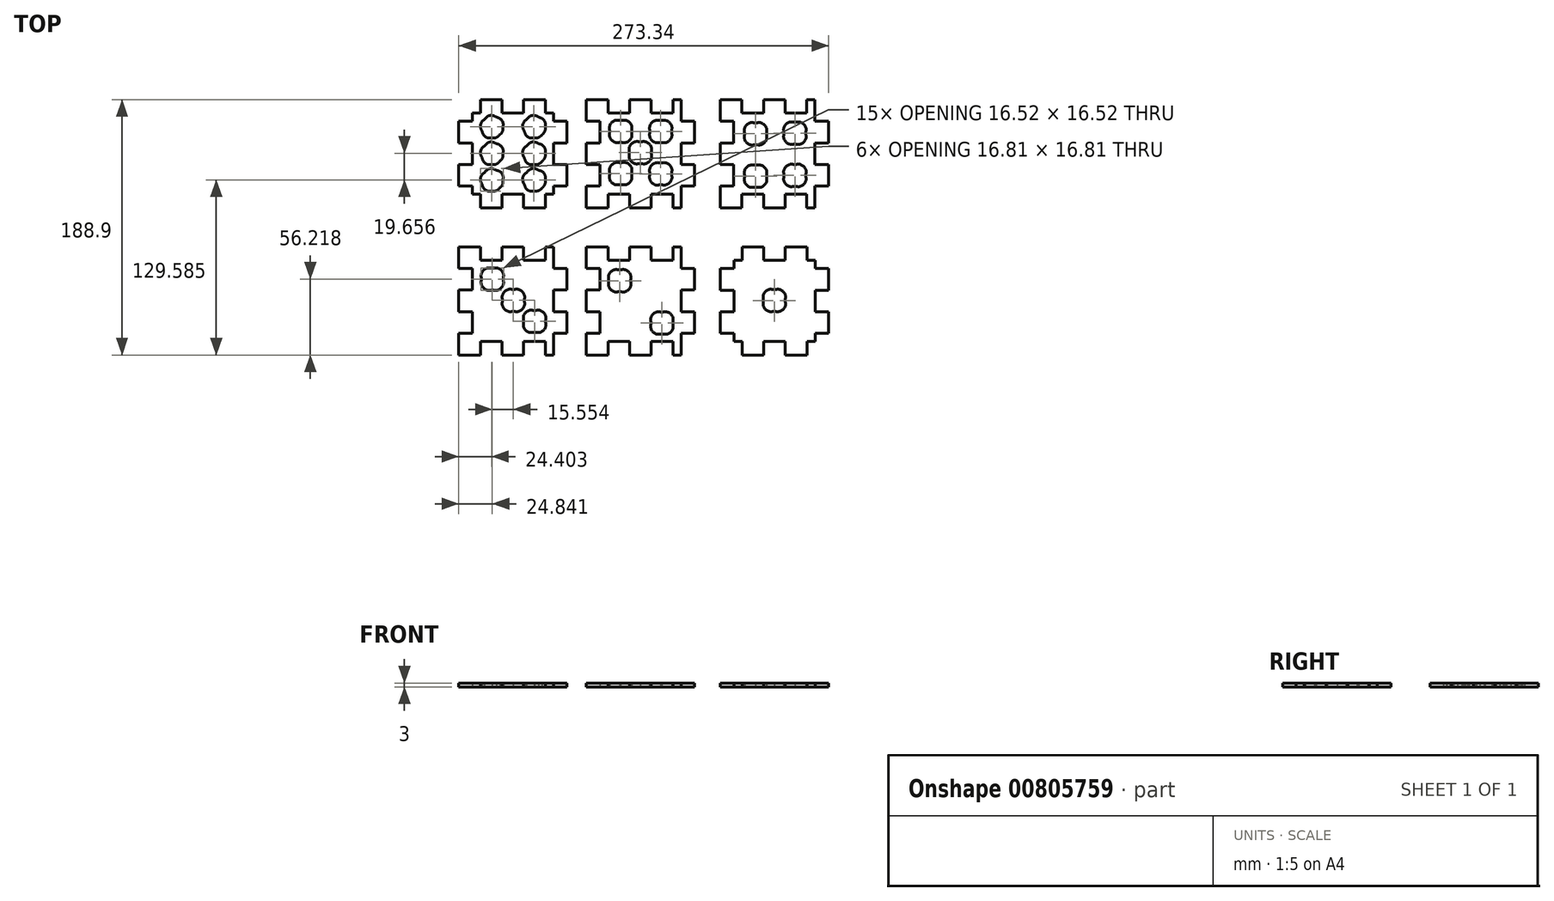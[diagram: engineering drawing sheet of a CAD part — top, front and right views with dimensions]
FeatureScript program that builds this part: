
annotation { "Feature Type Name" : "Feature", "Feature Type Description" : "" }
export const myFeature = defineFeature(function(context is Context, id is Id, definition is map)
    precondition{}
    {
        {
            var Q0;
            Q0=qCreatedBy(makeId("Top.planeOp"),FACE);
            var sketch = newSketch(context, id + "F0", { "sketchPlane" : qUnion([Q0])});
            skLineSegment(sketch, "E0", {"start": v(-126.67, 24.45) * mm, "end": v(-120.67, 24.45) * mm});
            skLineSegment(sketch, "E1", {"start": v(-120.67, 24.45) * mm, "end": v(-120.67, 14.45) * mm});
            skLineSegment(sketch, "E2", {"start": v(-120.67, 14.45) * mm, "end": v(-104.67, 14.45) * mm});
            skLineSegment(sketch, "E3", {"start": v(-104.67, 24.45) * mm, "end": v(-104.67, 14.45) * mm});
            skLineSegment(sketch, "E4", {"start": v(-104.67, 24.45) * mm, "end": v(-88.67, 24.45) * mm});
            skLineSegment(sketch, "E5", {"start": v(-88.67, 24.45) * mm, "end": v(-88.67, 14.45) * mm});
            skLineSegment(sketch, "E6", {"start": v(-88.67, 14.45) * mm, "end": v(-72.67, 14.45) * mm});
            skLineSegment(sketch, "E7", {"start": v(-72.67, 24.45) * mm, "end": v(-72.67, 14.45) * mm});
            skLineSegment(sketch, "E8", {"start": v(-72.67, 24.45) * mm, "end": v(-66.67, 24.45) * mm});
            skLineSegment(sketch, "E9", {"start": v(-126.67, 84.45) * mm, "end": v(-120.67, 84.45) * mm});
            skLineSegment(sketch, "E10", {"start": v(-120.67, 94.45) * mm, "end": v(-120.67, 84.45) * mm});
            skLineSegment(sketch, "E11", {"start": v(-120.67, 94.45) * mm, "end": v(-104.67, 94.45) * mm});
            skLineSegment(sketch, "E12", {"start": v(-104.67, 94.45) * mm, "end": v(-104.67, 84.45) * mm});
            skLineSegment(sketch, "E13", {"start": v(-104.67, 84.45) * mm, "end": v(-88.67, 84.45) * mm});
            skLineSegment(sketch, "E14", {"start": v(-88.67, 94.45) * mm, "end": v(-88.67, 84.45) * mm});
            skLineSegment(sketch, "E15", {"start": v(-88.67, 94.45) * mm, "end": v(-72.67, 94.45) * mm});
            skLineSegment(sketch, "E16", {"start": v(-72.67, 94.45) * mm, "end": v(-72.67, 84.45) * mm});
            skLineSegment(sketch, "E17", {"start": v(-72.67, 84.45) * mm, "end": v(-66.67, 84.45) * mm});
            skLineSegment(sketch, "E18", {"start": v(-126.67, 24.45) * mm, "end": v(-126.67, 30.45) * mm});
            skLineSegment(sketch, "E19", {"start": v(-126.67, 30.45) * mm, "end": v(-136.67, 30.45) * mm});
            skLineSegment(sketch, "E20", {"start": v(-136.67, 30.45) * mm, "end": v(-136.67, 46.45) * mm});
            skLineSegment(sketch, "E21", {"start": v(-126.67, 46.45) * mm, "end": v(-136.67, 46.45) * mm});
            skLineSegment(sketch, "E22", {"start": v(-126.67, 46.45) * mm, "end": v(-126.67, 62.45) * mm});
            skLineSegment(sketch, "E23", {"start": v(-126.67, 62.45) * mm, "end": v(-136.67, 62.45) * mm});
            skLineSegment(sketch, "E24", {"start": v(-136.67, 62.45) * mm, "end": v(-136.67, 78.45) * mm});
            skLineSegment(sketch, "E25", {"start": v(-126.67, 78.45) * mm, "end": v(-136.67, 78.45) * mm});
            skLineSegment(sketch, "E26", {"start": v(-126.67, 78.45) * mm, "end": v(-126.67, 84.45) * mm});
            skLineSegment(sketch, "E27", {"start": v(-66.67, 24.45) * mm, "end": v(-66.67, 30.45) * mm});
            skLineSegment(sketch, "E28", {"start": v(-56.67, 30.45) * mm, "end": v(-66.67, 30.45) * mm});
            skLineSegment(sketch, "E29", {"start": v(-56.67, 30.45) * mm, "end": v(-56.67, 46.45) * mm});
            skLineSegment(sketch, "E30", {"start": v(-56.67, 46.45) * mm, "end": v(-66.67, 46.45) * mm});
            skLineSegment(sketch, "E31", {"start": v(-66.67, 46.45) * mm, "end": v(-66.67, 62.45) * mm});
            skLineSegment(sketch, "E32", {"start": v(-56.67, 62.45) * mm, "end": v(-66.67, 62.45) * mm});
            skFitSpline(sketch, "E33", {"points": [v(-104, 74.18) * mm, v(-104, 72.06) * mm, v(-104.84, 70.02) * mm, v(-106.34, 68.52) * mm]});
            skFitSpline(sketch, "E34", {"points": [v(-106.34, 68.52) * mm, v(-107.84, 67.02) * mm, v(-109.88, 66.18) * mm, v(-112, 66.18) * mm]});
            skFitSpline(sketch, "E35", {"points": [v(-112, 66.18) * mm, v(-115.23, 66.18) * mm, v(-118.15, 68.13) * mm, v(-119.39, 71.12) * mm]});
            skFitSpline(sketch, "E36", {"points": [v(-119.39, 71.12) * mm, v(-120.63, 74.1) * mm, v(-119.94, 77.55) * mm, v(-117.66, 79.84) * mm]});
            skFitSpline(sketch, "E37", {"points": [v(-117.66, 79.84) * mm, v(-115.37, 82.12) * mm, v(-111.93, 82.8) * mm, v(-108.94, 81.57) * mm]});
            skFitSpline(sketch, "E38", {"points": [v(-108.94, 81.57) * mm, v(-105.95, 80.33) * mm, v(-104, 77.41) * mm, v(-104, 74.18) * mm]});
            skLineSegment(sketch, "E39", {"start": v(-56.67, 62.45) * mm, "end": v(-56.67, 78.45) * mm});
            skLineSegment(sketch, "E40", {"start": v(-56.67, 78.45) * mm, "end": v(-66.67, 78.45) * mm});
            skLineSegment(sketch, "E41", {"start": v(-66.67, 78.45) * mm, "end": v(-66.67, 84.45) * mm});
            skFitSpline(sketch, "E42", {"points": [v(-104, 34.87) * mm, v(-104, 32.74) * mm, v(-104.84, 30.7) * mm, v(-106.34, 29.2) * mm]});
            skFitSpline(sketch, "E43", {"points": [v(-106.34, 29.2) * mm, v(-107.84, 27.7) * mm, v(-109.88, 26.87) * mm, v(-112, 26.87) * mm]});
            skFitSpline(sketch, "E44", {"points": [v(-112, 26.87) * mm, v(-115.23, 26.87) * mm, v(-118.15, 28.82) * mm, v(-119.39, 31.8) * mm]});
            skFitSpline(sketch, "E45", {"points": [v(-119.39, 31.8) * mm, v(-120.63, 34.8) * mm, v(-119.94, 38.24) * mm, v(-117.66, 40.52) * mm]});
            skFitSpline(sketch, "E46", {"points": [v(-117.66, 40.52) * mm, v(-115.37, 42.81) * mm, v(-111.93, 43.5) * mm, v(-108.94, 42.26) * mm]});
            skFitSpline(sketch, "E47", {"points": [v(-108.94, 42.26) * mm, v(-105.95, 41.02) * mm, v(-104, 38.1) * mm, v(-104, 34.87) * mm]});
            skFitSpline(sketch, "E48", {"points": [v(-104, 54.52) * mm, v(-104, 52.4) * mm, v(-104.84, 50.37) * mm, v(-106.34, 48.87) * mm]});
            skFitSpline(sketch, "E49", {"points": [v(-106.34, 48.87) * mm, v(-107.84, 47.37) * mm, v(-109.88, 46.52) * mm, v(-112, 46.52) * mm]});
            skFitSpline(sketch, "E50", {"points": [v(-112, 46.52) * mm, v(-115.23, 46.52) * mm, v(-118.15, 48.47) * mm, v(-119.39, 51.46) * mm]});
            skFitSpline(sketch, "E51", {"points": [v(-119.39, 51.46) * mm, v(-120.63, 54.45) * mm, v(-119.94, 57.9) * mm, v(-117.66, 60.18) * mm]});
            skFitSpline(sketch, "E52", {"points": [v(-117.66, 60.18) * mm, v(-115.37, 62.47) * mm, v(-111.93, 63.15) * mm, v(-108.94, 61.91) * mm]});
            skFitSpline(sketch, "E53", {"points": [v(-108.94, 61.91) * mm, v(-105.95, 60.68) * mm, v(-104, 57.76) * mm, v(-104, 54.52) * mm]});
            skFitSpline(sketch, "E54", {"points": [v(-72.78, 74.18) * mm, v(-72.78, 72.06) * mm, v(-73.63, 70.02) * mm, v(-75.13, 68.52) * mm]});
            skFitSpline(sketch, "E55", {"points": [v(-75.13, 68.52) * mm, v(-76.63, 67.02) * mm, v(-78.66, 66.18) * mm, v(-80.78, 66.18) * mm]});
            skFitSpline(sketch, "E56", {"points": [v(-80.78, 66.18) * mm, v(-84.02, 66.18) * mm, v(-86.94, 68.13) * mm, v(-88.17, 71.12) * mm]});
            skFitSpline(sketch, "E57", {"points": [v(-88.17, 71.12) * mm, v(-89.41, 74.1) * mm, v(-88.73, 77.55) * mm, v(-86.44, 79.84) * mm]});
            skFitSpline(sketch, "E58", {"points": [v(-86.44, 79.84) * mm, v(-84.15, 82.12) * mm, v(-80.71, 82.8) * mm, v(-77.72, 81.57) * mm]});
            skFitSpline(sketch, "E59", {"points": [v(-77.72, 81.57) * mm, v(-74.73, 80.33) * mm, v(-72.78, 77.41) * mm, v(-72.78, 74.18) * mm]});
            skFitSpline(sketch, "E60", {"points": [v(-72.78, 34.87) * mm, v(-72.78, 32.74) * mm, v(-73.63, 30.7) * mm, v(-75.13, 29.2) * mm]});
            skFitSpline(sketch, "E61", {"points": [v(-75.13, 29.2) * mm, v(-76.63, 27.7) * mm, v(-78.66, 26.87) * mm, v(-80.78, 26.87) * mm]});
            skFitSpline(sketch, "E62", {"points": [v(-80.78, 26.87) * mm, v(-84.02, 26.87) * mm, v(-86.94, 28.82) * mm, v(-88.17, 31.8) * mm]});
            skFitSpline(sketch, "E63", {"points": [v(-88.17, 31.8) * mm, v(-89.41, 34.8) * mm, v(-88.73, 38.24) * mm, v(-86.44, 40.52) * mm]});
            skFitSpline(sketch, "E64", {"points": [v(-86.44, 40.52) * mm, v(-84.15, 42.81) * mm, v(-80.71, 43.5) * mm, v(-77.72, 42.26) * mm]});
            skFitSpline(sketch, "E65", {"points": [v(-77.72, 42.26) * mm, v(-74.73, 41.02) * mm, v(-72.78, 38.1) * mm, v(-72.78, 34.87) * mm]});
            skFitSpline(sketch, "E66", {"points": [v(-72.78, 54.52) * mm, v(-72.78, 52.4) * mm, v(-73.63, 50.37) * mm, v(-75.13, 48.87) * mm]});
            skFitSpline(sketch, "E67", {"points": [v(-75.13, 48.87) * mm, v(-76.63, 47.37) * mm, v(-78.66, 46.52) * mm, v(-80.78, 46.52) * mm]});
            skFitSpline(sketch, "E68", {"points": [v(-80.78, 46.52) * mm, v(-84.02, 46.52) * mm, v(-86.94, 48.47) * mm, v(-88.17, 51.46) * mm]});
            skFitSpline(sketch, "E69", {"points": [v(-88.17, 51.46) * mm, v(-89.41, 54.45) * mm, v(-88.73, 57.9) * mm, v(-86.44, 60.18) * mm]});
            skFitSpline(sketch, "E70", {"points": [v(-86.44, 60.18) * mm, v(-84.15, 62.47) * mm, v(-80.71, 63.15) * mm, v(-77.72, 61.91) * mm]});
            skFitSpline(sketch, "E71", {"points": [v(-77.72, 61.91) * mm, v(-74.73, 60.68) * mm, v(-72.78, 57.76) * mm, v(-72.78, 54.52) * mm]});
            skLineSegment(sketch, "E72", {"start": v(56.58, 14.45) * mm, "end": v(72.58, 14.45) * mm});
            skLineSegment(sketch, "E73", {"start": v(72.58, 24.45) * mm, "end": v(72.58, 14.45) * mm});
            skLineSegment(sketch, "E74", {"start": v(72.58, 24.45) * mm, "end": v(88.58, 24.45) * mm});
            skLineSegment(sketch, "E75", {"start": v(88.58, 24.45) * mm, "end": v(88.58, 14.45) * mm});
            skLineSegment(sketch, "E76", {"start": v(88.58, 14.45) * mm, "end": v(104.58, 14.45) * mm});
            skLineSegment(sketch, "E77", {"start": v(104.58, 24.45) * mm, "end": v(104.58, 14.45) * mm});
            skLineSegment(sketch, "E78", {"start": v(104.58, 24.45) * mm, "end": v(120.58, 24.45) * mm});
            skLineSegment(sketch, "E79", {"start": v(120.58, 24.45) * mm, "end": v(120.58, 14.45) * mm});
            skLineSegment(sketch, "E80", {"start": v(120.58, 14.45) * mm, "end": v(126.58, 14.45) * mm});
            skLineSegment(sketch, "E81", {"start": v(56.58, 94.45) * mm, "end": v(72.58, 94.45) * mm});
            skLineSegment(sketch, "E82", {"start": v(72.58, 94.45) * mm, "end": v(72.58, 84.45) * mm});
            skLineSegment(sketch, "E83", {"start": v(72.58, 84.45) * mm, "end": v(88.58, 84.45) * mm});
            skLineSegment(sketch, "E84", {"start": v(88.58, 94.45) * mm, "end": v(88.58, 84.45) * mm});
            skLineSegment(sketch, "E85", {"start": v(88.58, 94.45) * mm, "end": v(104.58, 94.45) * mm});
            skLineSegment(sketch, "E86", {"start": v(104.58, 94.45) * mm, "end": v(104.58, 84.45) * mm});
            skLineSegment(sketch, "E87", {"start": v(104.58, 84.45) * mm, "end": v(120.58, 84.45) * mm});
            skLineSegment(sketch, "E88", {"start": v(120.58, 94.45) * mm, "end": v(120.58, 84.45) * mm});
            skLineSegment(sketch, "E89", {"start": v(120.58, 94.45) * mm, "end": v(126.58, 94.45) * mm});
            skLineSegment(sketch, "E90", {"start": v(56.58, 14.45) * mm, "end": v(56.58, 30.45) * mm});
            skLineSegment(sketch, "E91", {"start": v(66.58, 30.45) * mm, "end": v(56.58, 30.45) * mm});
            skLineSegment(sketch, "E92", {"start": v(66.58, 30.45) * mm, "end": v(66.58, 46.45) * mm});
            skLineSegment(sketch, "E93", {"start": v(66.58, 46.45) * mm, "end": v(56.58, 46.45) * mm});
            skLineSegment(sketch, "E94", {"start": v(56.58, 46.45) * mm, "end": v(56.58, 62.45) * mm});
            skLineSegment(sketch, "E95", {"start": v(66.58, 62.45) * mm, "end": v(56.58, 62.45) * mm});
            skLineSegment(sketch, "E96", {"start": v(66.58, 62.45) * mm, "end": v(66.58, 78.45) * mm});
            skLineSegment(sketch, "E97", {"start": v(66.58, 78.45) * mm, "end": v(56.58, 78.45) * mm});
            skLineSegment(sketch, "E98", {"start": v(56.58, 78.45) * mm, "end": v(56.58, 94.45) * mm});
            skLineSegment(sketch, "E99", {"start": v(126.58, 14.45) * mm, "end": v(126.58, 30.45) * mm});
            skLineSegment(sketch, "E100", {"start": v(136.58, 30.45) * mm, "end": v(126.58, 30.45) * mm});
            skLineSegment(sketch, "E101", {"start": v(136.58, 30.45) * mm, "end": v(136.58, 46.45) * mm});
            skLineSegment(sketch, "E102", {"start": v(136.58, 46.45) * mm, "end": v(126.58, 46.45) * mm});
            skLineSegment(sketch, "E103", {"start": v(126.58, 46.45) * mm, "end": v(126.58, 62.45) * mm});
            skLineSegment(sketch, "E104", {"start": v(136.58, 62.45) * mm, "end": v(126.58, 62.45) * mm});
            skFitSpline(sketch, "E105", {"points": [v(90.66, 69.18) * mm, v(90.66, 64.77) * mm, v(87.07, 61.18) * mm, v(82.66, 61.18) * mm]});
            skFitSpline(sketch, "E106", {"points": [v(82.66, 61.18) * mm, v(78.24, 61.18) * mm, v(74.66, 64.77) * mm, v(74.66, 69.18) * mm]});
            skFitSpline(sketch, "E107", {"points": [v(74.66, 69.18) * mm, v(74.66, 73.6) * mm, v(78.24, 77.18) * mm, v(82.66, 77.18) * mm]});
            skFitSpline(sketch, "E108", {"points": [v(82.66, 77.18) * mm, v(87.07, 77.18) * mm, v(90.66, 73.6) * mm, v(90.66, 69.18) * mm]});
            skLineSegment(sketch, "E109", {"start": v(136.58, 62.45) * mm, "end": v(136.58, 78.45) * mm});
            skLineSegment(sketch, "E110", {"start": v(136.58, 78.45) * mm, "end": v(126.58, 78.45) * mm});
            skLineSegment(sketch, "E111", {"start": v(126.58, 78.45) * mm, "end": v(126.58, 94.45) * mm});
            skFitSpline(sketch, "E112", {"points": [v(90.66, 37.87) * mm, v(90.66, 33.45) * mm, v(87.07, 29.87) * mm, v(82.66, 29.87) * mm]});
            skFitSpline(sketch, "E113", {"points": [v(82.66, 29.87) * mm, v(78.24, 29.87) * mm, v(74.66, 33.45) * mm, v(74.66, 37.87) * mm]});
            skFitSpline(sketch, "E114", {"points": [v(74.66, 37.87) * mm, v(74.66, 42.29) * mm, v(78.24, 45.87) * mm, v(82.66, 45.87) * mm]});
            skFitSpline(sketch, "E115", {"points": [v(82.66, 45.87) * mm, v(87.07, 45.87) * mm, v(90.66, 42.29) * mm, v(90.66, 37.87) * mm]});
            skFitSpline(sketch, "E116", {"points": [v(119.73, 69.7) * mm, v(119.73, 65.28) * mm, v(116.15, 61.7) * mm, v(111.73, 61.7) * mm]});
            skFitSpline(sketch, "E117", {"points": [v(111.73, 61.7) * mm, v(107.31, 61.7) * mm, v(103.73, 65.28) * mm, v(103.73, 69.7) * mm]});
            skFitSpline(sketch, "E118", {"points": [v(103.73, 69.7) * mm, v(103.73, 74.11) * mm, v(107.31, 77.7) * mm, v(111.73, 77.7) * mm]});
            skFitSpline(sketch, "E119", {"points": [v(111.73, 77.7) * mm, v(116.15, 77.7) * mm, v(119.73, 74.11) * mm, v(119.73, 69.7) * mm]});
            skFitSpline(sketch, "E120", {"points": [v(119.73, 38.38) * mm, v(119.73, 33.96) * mm, v(116.15, 30.38) * mm, v(111.73, 30.38) * mm]});
            skFitSpline(sketch, "E121", {"points": [v(111.73, 30.38) * mm, v(107.31, 30.38) * mm, v(103.73, 33.96) * mm, v(103.73, 38.38) * mm]});
            skFitSpline(sketch, "E122", {"points": [v(103.73, 38.38) * mm, v(103.73, 42.8) * mm, v(107.31, 46.38) * mm, v(111.73, 46.38) * mm]});
            skFitSpline(sketch, "E123", {"points": [v(111.73, 46.38) * mm, v(116.15, 46.38) * mm, v(119.73, 42.8) * mm, v(119.73, 38.38) * mm]});
            skLineSegment(sketch, "E124", {"start": v(-42.35, -94.36) * mm, "end": v(-26.35, -94.36) * mm});
            skLineSegment(sketch, "E125", {"start": v(-26.35, -84.36) * mm, "end": v(-26.35, -94.36) * mm});
            skLineSegment(sketch, "E126", {"start": v(-26.35, -84.36) * mm, "end": v(-10.35, -84.36) * mm});
            skLineSegment(sketch, "E127", {"start": v(-10.35, -84.36) * mm, "end": v(-10.35, -94.36) * mm});
            skLineSegment(sketch, "E128", {"start": v(-10.35, -94.36) * mm, "end": v(5.65, -94.36) * mm});
            skLineSegment(sketch, "E129", {"start": v(5.65, -84.36) * mm, "end": v(5.65, -94.36) * mm});
            skLineSegment(sketch, "E130", {"start": v(5.65, -84.36) * mm, "end": v(21.65, -84.36) * mm});
            skLineSegment(sketch, "E131", {"start": v(21.65, -84.36) * mm, "end": v(21.65, -94.36) * mm});
            skLineSegment(sketch, "E132", {"start": v(21.65, -94.36) * mm, "end": v(27.65, -94.36) * mm});
            skLineSegment(sketch, "E133", {"start": v(-42.35, -14.36) * mm, "end": v(-26.35, -14.36) * mm});
            skLineSegment(sketch, "E134", {"start": v(-26.35, -14.36) * mm, "end": v(-26.35, -24.36) * mm});
            skLineSegment(sketch, "E135", {"start": v(-26.35, -24.36) * mm, "end": v(-10.35, -24.36) * mm});
            skLineSegment(sketch, "E136", {"start": v(-10.35, -14.36) * mm, "end": v(-10.35, -24.36) * mm});
            skLineSegment(sketch, "E137", {"start": v(-10.35, -14.36) * mm, "end": v(5.65, -14.36) * mm});
            skLineSegment(sketch, "E138", {"start": v(5.65, -14.36) * mm, "end": v(5.65, -24.36) * mm});
            skLineSegment(sketch, "E139", {"start": v(5.65, -24.36) * mm, "end": v(21.65, -24.36) * mm});
            skLineSegment(sketch, "E140", {"start": v(21.65, -14.36) * mm, "end": v(21.65, -24.36) * mm});
            skLineSegment(sketch, "E141", {"start": v(21.65, -14.36) * mm, "end": v(27.65, -14.36) * mm});
            skLineSegment(sketch, "E142", {"start": v(-42.35, -94.36) * mm, "end": v(-42.35, -78.36) * mm});
            skLineSegment(sketch, "E143", {"start": v(-32.35, -78.36) * mm, "end": v(-42.35, -78.36) * mm});
            skLineSegment(sketch, "E144", {"start": v(-32.35, -78.36) * mm, "end": v(-32.35, -62.36) * mm});
            skLineSegment(sketch, "E145", {"start": v(-32.35, -62.36) * mm, "end": v(-42.35, -62.36) * mm});
            skLineSegment(sketch, "E146", {"start": v(-42.35, -62.36) * mm, "end": v(-42.35, -46.36) * mm});
            skLineSegment(sketch, "E147", {"start": v(-32.35, -46.36) * mm, "end": v(-42.35, -46.36) * mm});
            skLineSegment(sketch, "E148", {"start": v(-32.35, -46.36) * mm, "end": v(-32.35, -30.36) * mm});
            skLineSegment(sketch, "E149", {"start": v(-32.35, -30.36) * mm, "end": v(-42.35, -30.36) * mm});
            skLineSegment(sketch, "E150", {"start": v(-42.35, -30.36) * mm, "end": v(-42.35, -14.36) * mm});
            skLineSegment(sketch, "E151", {"start": v(27.65, -94.36) * mm, "end": v(27.65, -78.36) * mm});
            skLineSegment(sketch, "E152", {"start": v(37.65, -78.36) * mm, "end": v(27.65, -78.36) * mm});
            skLineSegment(sketch, "E153", {"start": v(37.65, -78.36) * mm, "end": v(37.65, -62.36) * mm});
            skLineSegment(sketch, "E154", {"start": v(37.65, -62.36) * mm, "end": v(27.65, -62.36) * mm});
            skLineSegment(sketch, "E155", {"start": v(27.65, -62.36) * mm, "end": v(27.65, -46.36) * mm});
            skLineSegment(sketch, "E156", {"start": v(37.65, -46.36) * mm, "end": v(27.65, -46.36) * mm});
            skFitSpline(sketch, "E157", {"points": [v(-9.71, -39.47) * mm, v(-9.71, -43.89) * mm, v(-13.3, -47.47) * mm, v(-17.71, -47.47) * mm]});
            skFitSpline(sketch, "E158", {"points": [v(-17.71, -47.47) * mm, v(-22.13, -47.47) * mm, v(-25.71, -43.89) * mm, v(-25.71, -39.47) * mm]});
            skFitSpline(sketch, "E159", {"points": [v(-25.71, -39.47) * mm, v(-25.71, -35.05) * mm, v(-22.13, -31.47) * mm, v(-17.71, -31.47) * mm]});
            skFitSpline(sketch, "E160", {"points": [v(-17.71, -31.47) * mm, v(-13.3, -31.47) * mm, v(-9.71, -35.05) * mm, v(-9.71, -39.47) * mm]});
            skLineSegment(sketch, "E161", {"start": v(37.65, -46.36) * mm, "end": v(37.65, -30.36) * mm});
            skLineSegment(sketch, "E162", {"start": v(37.65, -30.36) * mm, "end": v(27.65, -30.36) * mm});
            skLineSegment(sketch, "E163", {"start": v(27.65, -30.36) * mm, "end": v(27.65, -14.36) * mm});
            skFitSpline(sketch, "E164", {"points": [v(21.5, -70.78) * mm, v(21.5, -75.2) * mm, v(17.92, -78.78) * mm, v(13.5, -78.78) * mm]});
            skFitSpline(sketch, "E165", {"points": [v(13.5, -78.78) * mm, v(9.08, -78.78) * mm, v(5.5, -75.2) * mm, v(5.5, -70.78) * mm]});
            skFitSpline(sketch, "E166", {"points": [v(5.5, -70.78) * mm, v(5.5, -66.36) * mm, v(9.08, -62.78) * mm, v(13.5, -62.78) * mm]});
            skFitSpline(sketch, "E167", {"points": [v(13.5, -62.78) * mm, v(17.92, -62.78) * mm, v(21.5, -66.36) * mm, v(21.5, -70.78) * mm]});
            skLineSegment(sketch, "E168", {"start": v(-42.35, 14.45) * mm, "end": v(-26.35, 14.45) * mm});
            skLineSegment(sketch, "E169", {"start": v(-26.35, 24.45) * mm, "end": v(-26.35, 14.45) * mm});
            skLineSegment(sketch, "E170", {"start": v(-26.35, 24.45) * mm, "end": v(-10.35, 24.45) * mm});
            skLineSegment(sketch, "E171", {"start": v(-10.35, 24.45) * mm, "end": v(-10.35, 14.45) * mm});
            skLineSegment(sketch, "E172", {"start": v(-10.35, 14.45) * mm, "end": v(5.65, 14.45) * mm});
            skLineSegment(sketch, "E173", {"start": v(5.65, 24.45) * mm, "end": v(5.65, 14.45) * mm});
            skLineSegment(sketch, "E174", {"start": v(5.65, 24.45) * mm, "end": v(21.65, 24.45) * mm});
            skLineSegment(sketch, "E175", {"start": v(21.65, 24.45) * mm, "end": v(21.65, 14.45) * mm});
            skLineSegment(sketch, "E176", {"start": v(21.65, 14.45) * mm, "end": v(27.65, 14.45) * mm});
            skLineSegment(sketch, "E177", {"start": v(-42.35, 94.45) * mm, "end": v(-26.35, 94.45) * mm});
            skLineSegment(sketch, "E178", {"start": v(-26.35, 94.45) * mm, "end": v(-26.35, 84.45) * mm});
            skLineSegment(sketch, "E179", {"start": v(-26.35, 84.45) * mm, "end": v(-10.35, 84.45) * mm});
            skLineSegment(sketch, "E180", {"start": v(-10.35, 94.45) * mm, "end": v(-10.35, 84.45) * mm});
            skLineSegment(sketch, "E181", {"start": v(-10.35, 94.45) * mm, "end": v(5.65, 94.45) * mm});
            skLineSegment(sketch, "E182", {"start": v(5.65, 94.45) * mm, "end": v(5.65, 84.45) * mm});
            skLineSegment(sketch, "E183", {"start": v(5.65, 84.45) * mm, "end": v(21.65, 84.45) * mm});
            skLineSegment(sketch, "E184", {"start": v(21.65, 94.45) * mm, "end": v(21.65, 84.45) * mm});
            skLineSegment(sketch, "E185", {"start": v(21.65, 94.45) * mm, "end": v(27.65, 94.45) * mm});
            skLineSegment(sketch, "E186", {"start": v(-42.35, 14.45) * mm, "end": v(-42.35, 30.45) * mm});
            skLineSegment(sketch, "E187", {"start": v(-32.35, 30.45) * mm, "end": v(-42.35, 30.45) * mm});
            skLineSegment(sketch, "E188", {"start": v(-32.35, 30.45) * mm, "end": v(-32.35, 46.45) * mm});
            skLineSegment(sketch, "E189", {"start": v(-32.35, 46.45) * mm, "end": v(-42.35, 46.45) * mm});
            skLineSegment(sketch, "E190", {"start": v(-42.35, 46.45) * mm, "end": v(-42.35, 62.45) * mm});
            skLineSegment(sketch, "E191", {"start": v(-32.35, 62.45) * mm, "end": v(-42.35, 62.45) * mm});
            skLineSegment(sketch, "E192", {"start": v(-32.35, 62.45) * mm, "end": v(-32.35, 78.45) * mm});
            skLineSegment(sketch, "E193", {"start": v(-32.35, 78.45) * mm, "end": v(-42.35, 78.45) * mm});
            skLineSegment(sketch, "E194", {"start": v(-42.35, 78.45) * mm, "end": v(-42.35, 94.45) * mm});
            skLineSegment(sketch, "E195", {"start": v(27.65, 14.45) * mm, "end": v(27.65, 30.45) * mm});
            skLineSegment(sketch, "E196", {"start": v(37.65, 30.45) * mm, "end": v(27.65, 30.45) * mm});
            skLineSegment(sketch, "E197", {"start": v(37.65, 30.45) * mm, "end": v(37.65, 46.45) * mm});
            skLineSegment(sketch, "E198", {"start": v(37.65, 46.45) * mm, "end": v(27.65, 46.45) * mm});
            skLineSegment(sketch, "E199", {"start": v(27.65, 46.45) * mm, "end": v(27.65, 62.45) * mm});
            skLineSegment(sketch, "E200", {"start": v(37.65, 62.45) * mm, "end": v(27.65, 62.45) * mm});
            skFitSpline(sketch, "E201", {"points": [v(-8.97, 71) * mm, v(-8.97, 66.58) * mm, v(-12.55, 63) * mm, v(-16.97, 63) * mm]});
            skFitSpline(sketch, "E202", {"points": [v(-16.97, 63) * mm, v(-21.39, 63) * mm, v(-24.97, 66.58) * mm, v(-24.97, 71) * mm]});
            skFitSpline(sketch, "E203", {"points": [v(-24.97, 71) * mm, v(-24.97, 75.41) * mm, v(-21.39, 79) * mm, v(-16.97, 79) * mm]});
            skFitSpline(sketch, "E204", {"points": [v(-16.97, 79) * mm, v(-12.55, 79) * mm, v(-8.97, 75.41) * mm, v(-8.97, 71) * mm]});
            skLineSegment(sketch, "E205", {"start": v(37.65, 62.45) * mm, "end": v(37.65, 78.45) * mm});
            skLineSegment(sketch, "E206", {"start": v(37.65, 78.45) * mm, "end": v(27.65, 78.45) * mm});
            skLineSegment(sketch, "E207", {"start": v(27.65, 78.45) * mm, "end": v(27.65, 94.45) * mm});
            skFitSpline(sketch, "E208", {"points": [v(-8.97, 39.68) * mm, v(-8.97, 35.26) * mm, v(-12.55, 31.68) * mm, v(-16.97, 31.68) * mm]});
            skFitSpline(sketch, "E209", {"points": [v(-16.97, 31.68) * mm, v(-21.39, 31.68) * mm, v(-24.97, 35.26) * mm, v(-24.97, 39.68) * mm]});
            skFitSpline(sketch, "E210", {"points": [v(-24.97, 39.68) * mm, v(-24.97, 44.1) * mm, v(-21.39, 47.68) * mm, v(-16.97, 47.68) * mm]});
            skFitSpline(sketch, "E211", {"points": [v(-16.97, 47.68) * mm, v(-12.55, 47.68) * mm, v(-8.97, 44.1) * mm, v(-8.97, 39.68) * mm]});
            skFitSpline(sketch, "E212", {"points": [v(20.61, 70.9) * mm, v(20.61, 66.47) * mm, v(17.03, 62.9) * mm, v(12.61, 62.9) * mm]});
            skFitSpline(sketch, "E213", {"points": [v(12.61, 62.9) * mm, v(8.2, 62.9) * mm, v(4.61, 66.47) * mm, v(4.61, 70.9) * mm]});
            skFitSpline(sketch, "E214", {"points": [v(4.61, 70.9) * mm, v(4.61, 75.3) * mm, v(8.2, 78.9) * mm, v(12.61, 78.9) * mm]});
            skFitSpline(sketch, "E215", {"points": [v(12.61, 78.9) * mm, v(17.03, 78.9) * mm, v(20.61, 75.3) * mm, v(20.61, 70.9) * mm]});
            skFitSpline(sketch, "E216", {"points": [v(20.61, 39.58) * mm, v(20.61, 35.16) * mm, v(17.03, 31.58) * mm, v(12.61, 31.58) * mm]});
            skFitSpline(sketch, "E217", {"points": [v(12.61, 31.58) * mm, v(8.2, 31.58) * mm, v(4.61, 35.16) * mm, v(4.61, 39.58) * mm]});
            skFitSpline(sketch, "E218", {"points": [v(4.61, 39.58) * mm, v(4.61, 44) * mm, v(8.2, 47.58) * mm, v(12.61, 47.58) * mm]});
            skFitSpline(sketch, "E219", {"points": [v(12.61, 47.58) * mm, v(17.03, 47.58) * mm, v(20.61, 44) * mm, v(20.61, 39.58) * mm]});
            skFitSpline(sketch, "E220", {"points": [v(5.52, 55.2) * mm, v(5.52, 50.78) * mm, v(1.94, 47.2) * mm, v(-2.48, 47.2) * mm]});
            skFitSpline(sketch, "E221", {"points": [v(-2.48, 47.2) * mm, v(-6.9, 47.2) * mm, v(-10.48, 50.78) * mm, v(-10.48, 55.2) * mm]});
            skFitSpline(sketch, "E222", {"points": [v(-10.48, 55.2) * mm, v(-10.48, 59.61) * mm, v(-6.9, 63.2) * mm, v(-2.48, 63.2) * mm]});
            skFitSpline(sketch, "E223", {"points": [v(-2.48, 63.2) * mm, v(1.94, 63.2) * mm, v(5.52, 59.61) * mm, v(5.52, 55.2) * mm]});
            skLineSegment(sketch, "E224", {"start": v(-136.67, -94.36) * mm, "end": v(-120.67, -94.36) * mm});
            skLineSegment(sketch, "E225", {"start": v(-120.67, -84.36) * mm, "end": v(-120.67, -94.36) * mm});
            skLineSegment(sketch, "E226", {"start": v(-120.67, -84.36) * mm, "end": v(-104.67, -84.36) * mm});
            skLineSegment(sketch, "E227", {"start": v(-104.67, -84.36) * mm, "end": v(-104.67, -94.36) * mm});
            skLineSegment(sketch, "E228", {"start": v(-104.67, -94.36) * mm, "end": v(-88.67, -94.36) * mm});
            skLineSegment(sketch, "E229", {"start": v(-88.67, -84.36) * mm, "end": v(-88.67, -94.36) * mm});
            skLineSegment(sketch, "E230", {"start": v(-88.67, -84.36) * mm, "end": v(-72.67, -84.36) * mm});
            skLineSegment(sketch, "E231", {"start": v(-72.67, -84.36) * mm, "end": v(-72.67, -94.36) * mm});
            skLineSegment(sketch, "E232", {"start": v(-72.67, -94.36) * mm, "end": v(-66.67, -94.36) * mm});
            skLineSegment(sketch, "E233", {"start": v(-136.67, -14.36) * mm, "end": v(-120.67, -14.36) * mm});
            skLineSegment(sketch, "E234", {"start": v(-120.67, -14.36) * mm, "end": v(-120.67, -24.36) * mm});
            skLineSegment(sketch, "E235", {"start": v(-120.67, -24.36) * mm, "end": v(-104.67, -24.36) * mm});
            skLineSegment(sketch, "E236", {"start": v(-104.67, -14.36) * mm, "end": v(-104.67, -24.36) * mm});
            skLineSegment(sketch, "E237", {"start": v(-104.67, -14.36) * mm, "end": v(-88.67, -14.36) * mm});
            skLineSegment(sketch, "E238", {"start": v(-88.67, -14.36) * mm, "end": v(-88.67, -24.36) * mm});
            skLineSegment(sketch, "E239", {"start": v(-88.67, -24.36) * mm, "end": v(-72.67, -24.36) * mm});
            skLineSegment(sketch, "E240", {"start": v(-72.67, -14.36) * mm, "end": v(-72.67, -24.36) * mm});
            skLineSegment(sketch, "E241", {"start": v(-72.67, -14.36) * mm, "end": v(-66.67, -14.36) * mm});
            skLineSegment(sketch, "E242", {"start": v(-136.67, -94.36) * mm, "end": v(-136.67, -78.36) * mm});
            skLineSegment(sketch, "E243", {"start": v(-126.67, -78.36) * mm, "end": v(-136.67, -78.36) * mm});
            skLineSegment(sketch, "E244", {"start": v(-126.67, -78.36) * mm, "end": v(-126.67, -62.36) * mm});
            skLineSegment(sketch, "E245", {"start": v(-126.67, -62.36) * mm, "end": v(-136.67, -62.36) * mm});
            skLineSegment(sketch, "E246", {"start": v(-136.67, -62.36) * mm, "end": v(-136.67, -46.36) * mm});
            skLineSegment(sketch, "E247", {"start": v(-126.67, -46.36) * mm, "end": v(-136.67, -46.36) * mm});
            skLineSegment(sketch, "E248", {"start": v(-126.67, -46.36) * mm, "end": v(-126.67, -30.36) * mm});
            skLineSegment(sketch, "E249", {"start": v(-126.67, -30.36) * mm, "end": v(-136.67, -30.36) * mm});
            skLineSegment(sketch, "E250", {"start": v(-136.67, -30.36) * mm, "end": v(-136.67, -14.36) * mm});
            skLineSegment(sketch, "E251", {"start": v(-66.67, -94.36) * mm, "end": v(-66.67, -78.36) * mm});
            skLineSegment(sketch, "E252", {"start": v(-56.67, -78.36) * mm, "end": v(-66.67, -78.36) * mm});
            skLineSegment(sketch, "E253", {"start": v(-56.67, -78.36) * mm, "end": v(-56.67, -62.36) * mm});
            skLineSegment(sketch, "E254", {"start": v(-56.67, -62.36) * mm, "end": v(-66.67, -62.36) * mm});
            skLineSegment(sketch, "E255", {"start": v(-66.67, -62.36) * mm, "end": v(-66.67, -46.36) * mm});
            skLineSegment(sketch, "E256", {"start": v(-56.67, -46.36) * mm, "end": v(-66.67, -46.36) * mm});
            skFitSpline(sketch, "E257", {"points": [v(-103.83, -38.23) * mm, v(-103.83, -42.65) * mm, v(-107.41, -46.23) * mm, v(-111.83, -46.23) * mm]});
            skFitSpline(sketch, "E258", {"points": [v(-111.83, -46.23) * mm, v(-116.25, -46.23) * mm, v(-119.83, -42.65) * mm, v(-119.83, -38.23) * mm]});
            skFitSpline(sketch, "E259", {"points": [v(-119.83, -38.23) * mm, v(-119.83, -33.81) * mm, v(-116.25, -30.23) * mm, v(-111.83, -30.23) * mm]});
            skFitSpline(sketch, "E260", {"points": [v(-111.83, -30.23) * mm, v(-107.41, -30.23) * mm, v(-103.83, -33.81) * mm, v(-103.83, -38.23) * mm]});
            skLineSegment(sketch, "E261", {"start": v(-56.67, -46.36) * mm, "end": v(-56.67, -30.36) * mm});
            skLineSegment(sketch, "E262", {"start": v(-56.67, -30.36) * mm, "end": v(-66.67, -30.36) * mm});
            skLineSegment(sketch, "E263", {"start": v(-66.67, -30.36) * mm, "end": v(-66.67, -14.36) * mm});
            skFitSpline(sketch, "E264", {"points": [v(-72.61, -69.54) * mm, v(-72.61, -73.96) * mm, v(-76.2, -77.54) * mm, v(-80.61, -77.54) * mm]});
            skFitSpline(sketch, "E265", {"points": [v(-80.61, -77.54) * mm, v(-85.03, -77.54) * mm, v(-88.61, -73.96) * mm, v(-88.61, -69.54) * mm]});
            skFitSpline(sketch, "E266", {"points": [v(-88.61, -69.54) * mm, v(-88.61, -65.13) * mm, v(-85.03, -61.54) * mm, v(-80.61, -61.54) * mm]});
            skFitSpline(sketch, "E267", {"points": [v(-80.61, -61.54) * mm, v(-76.2, -61.54) * mm, v(-72.61, -65.13) * mm, v(-72.61, -69.54) * mm]});
            skFitSpline(sketch, "E268", {"points": [v(-88.27, -54.04) * mm, v(-88.27, -58.46) * mm, v(-91.86, -62.04) * mm, v(-96.27, -62.04) * mm]});
            skFitSpline(sketch, "E269", {"points": [v(-96.27, -62.04) * mm, v(-100.7, -62.04) * mm, v(-104.27, -58.46) * mm, v(-104.27, -54.04) * mm]});
            skFitSpline(sketch, "E270", {"points": [v(-104.27, -54.04) * mm, v(-104.27, -49.62) * mm, v(-100.7, -46.04) * mm, v(-96.27, -46.04) * mm]});
            skFitSpline(sketch, "E271", {"points": [v(-96.27, -46.04) * mm, v(-91.86, -46.04) * mm, v(-88.27, -49.62) * mm, v(-88.27, -54.04) * mm]});
            skLineSegment(sketch, "E272", {"start": v(66.67, -84.45) * mm, "end": v(72.67, -84.45) * mm});
            skLineSegment(sketch, "E273", {"start": v(72.67, -84.45) * mm, "end": v(72.67, -94.45) * mm});
            skLineSegment(sketch, "E274", {"start": v(72.67, -94.45) * mm, "end": v(88.67, -94.45) * mm});
            skLineSegment(sketch, "E275", {"start": v(88.67, -84.45) * mm, "end": v(88.67, -94.45) * mm});
            skLineSegment(sketch, "E276", {"start": v(88.67, -84.45) * mm, "end": v(104.67, -84.45) * mm});
            skLineSegment(sketch, "E277", {"start": v(104.67, -84.45) * mm, "end": v(104.67, -94.45) * mm});
            skLineSegment(sketch, "E278", {"start": v(104.67, -94.45) * mm, "end": v(120.67, -94.45) * mm});
            skLineSegment(sketch, "E279", {"start": v(120.67, -84.45) * mm, "end": v(120.67, -94.45) * mm});
            skLineSegment(sketch, "E280", {"start": v(120.67, -84.45) * mm, "end": v(126.67, -84.45) * mm});
            skLineSegment(sketch, "E281", {"start": v(66.67, -24.45) * mm, "end": v(72.67, -24.45) * mm});
            skLineSegment(sketch, "E282", {"start": v(72.67, -14.45) * mm, "end": v(72.67, -24.45) * mm});
            skLineSegment(sketch, "E283", {"start": v(72.67, -14.45) * mm, "end": v(88.67, -14.45) * mm});
            skLineSegment(sketch, "E284", {"start": v(88.67, -14.45) * mm, "end": v(88.67, -24.45) * mm});
            skLineSegment(sketch, "E285", {"start": v(88.67, -24.45) * mm, "end": v(104.67, -24.45) * mm});
            skLineSegment(sketch, "E286", {"start": v(104.67, -14.45) * mm, "end": v(104.67, -24.45) * mm});
            skLineSegment(sketch, "E287", {"start": v(104.67, -14.45) * mm, "end": v(120.67, -14.45) * mm});
            skLineSegment(sketch, "E288", {"start": v(120.67, -14.45) * mm, "end": v(120.67, -24.45) * mm});
            skLineSegment(sketch, "E289", {"start": v(120.67, -24.45) * mm, "end": v(126.67, -24.45) * mm});
            skLineSegment(sketch, "E290", {"start": v(66.67, -84.45) * mm, "end": v(66.67, -78.45) * mm});
            skLineSegment(sketch, "E291", {"start": v(66.67, -78.45) * mm, "end": v(56.67, -78.45) * mm});
            skLineSegment(sketch, "E292", {"start": v(56.67, -78.45) * mm, "end": v(56.67, -62.45) * mm});
            skLineSegment(sketch, "E293", {"start": v(66.67, -62.45) * mm, "end": v(56.67, -62.45) * mm});
            skLineSegment(sketch, "E294", {"start": v(66.67, -62.45) * mm, "end": v(66.67, -46.45) * mm});
            skLineSegment(sketch, "E295", {"start": v(66.67, -46.45) * mm, "end": v(56.67, -46.45) * mm});
            skLineSegment(sketch, "E296", {"start": v(56.67, -46.45) * mm, "end": v(56.67, -30.45) * mm});
            skLineSegment(sketch, "E297", {"start": v(66.67, -30.45) * mm, "end": v(56.67, -30.45) * mm});
            skLineSegment(sketch, "E298", {"start": v(66.67, -30.45) * mm, "end": v(66.67, -24.45) * mm});
            skLineSegment(sketch, "E299", {"start": v(126.67, -84.45) * mm, "end": v(126.67, -78.45) * mm});
            skLineSegment(sketch, "E300", {"start": v(136.67, -78.45) * mm, "end": v(126.67, -78.45) * mm});
            skLineSegment(sketch, "E301", {"start": v(136.67, -78.45) * mm, "end": v(136.67, -62.45) * mm});
            skLineSegment(sketch, "E302", {"start": v(136.67, -62.45) * mm, "end": v(126.67, -62.45) * mm});
            skLineSegment(sketch, "E303", {"start": v(126.67, -62.45) * mm, "end": v(126.67, -46.45) * mm});
            skLineSegment(sketch, "E304", {"start": v(136.67, -46.45) * mm, "end": v(126.67, -46.45) * mm});
            skFitSpline(sketch, "E305", {"points": [v(104.51, -54.07) * mm, v(104.51, -58.48) * mm, v(100.93, -62.07) * mm, v(96.51, -62.07) * mm]});
            skFitSpline(sketch, "E306", {"points": [v(96.51, -62.07) * mm, v(92.1, -62.07) * mm, v(88.51, -58.48) * mm, v(88.51, -54.07) * mm]});
            skFitSpline(sketch, "E307", {"points": [v(88.51, -54.07) * mm, v(88.51, -49.65) * mm, v(92.1, -46.07) * mm, v(96.51, -46.07) * mm]});
            skFitSpline(sketch, "E308", {"points": [v(96.51, -46.07) * mm, v(100.93, -46.07) * mm, v(104.51, -49.65) * mm, v(104.51, -54.07) * mm]});
            skLineSegment(sketch, "E309", {"start": v(136.67, -46.45) * mm, "end": v(136.67, -30.45) * mm});
            skLineSegment(sketch, "E310", {"start": v(136.67, -30.45) * mm, "end": v(126.67, -30.45) * mm});
            skLineSegment(sketch, "E311", {"start": v(126.67, -30.45) * mm, "end": v(126.67, -24.45) * mm});
            skSolve(sketch);
        }
        {
            var Q0;
            Q0 = qSketchRegion(id + "F0", true);
            extrude(context, id + "F1", {"entities" : qUnion([Q0]), "depth" : 3 * mm, "offsetDistance" : 25 * mm});
        }
    });
